# Revit family: 351_712 37 39
name_source: partatom
category: Plumbing Fixtures
revit_build: Autodesk Revit 2018 (Build: 20170223_1515(x64)
units: mm (PartAtom-declared; Revit-internal decimal feet)

## family parameters
Always vertical = Yes
Cut with Voids When Loaded = No
Part Type = Normal
Room Calculation Point = No
Round Connector Dimension = Use Diameter
Shared = No
Work Plane-Based = No

## types (1)
- ACO Golvbrunn 270 x 270 DN 75 Horizontal CB 9.5
    CAT0 = Yes
    CLBTZ = 0 mm  [stored 0 ft]
    CL_Location_5000 = 5000 mm  [stored 16.4042 ft]
    CT1 = No
    CT2 = Yes
    DC = 75 mm
    Description = ACO COLLECT BOX 9:5 EN1.4404 GULLY 270X270 H75 VINYL
    H2 = 60 mm  [stored 0.19685 ft]
    H4 = 8 mm  [stored 0.0262467 ft]
    H4_End__ve = -60 mm  [stored -0.19685 ft]
    H4__ve = -8 mm  [stored -0.0262467 ft]
    H5 = 52 mm  [stored 0.170604 ft]
    HTT = 157 mm  [stored 0.515092 ft]
    HTT__ve = -157 mm  [stored -0.515092 ft]
    LL = 130 mm  [stored 0.426509 ft]
    MC_Default_elevation = 0 mm  [stored 0 ft]
    Manufacturer = ACO Drain
    QmdConnectorList = 601;DC
    RR = 109 mm  [stored 0.357612 ft]
    WW = 130 mm  [stored 0.426509 ft]
    XRefLineVPlnId = 7453
    XX = 160 mm  [stored 0.524934 ft]
    YRefLineVPlnId = 7456
    YY = 160 mm  [stored 0.524934 ft]
    Z2 = 169 mm  [stored 0.554462 ft]
    magiPartTypeId = 351
    magiProductCode = ACO Golvbrunn 270 x 270 DN 75 Horizontal CB 9.5
    magiProductFamilyId = 712 37 39
    magiProductId = 712 37 39

note: [stored X ft] marks values corroborated as IEEE doubles in the binary element streams (Revit-internal decimal feet)

## geometry (parser evidence)
native form markers: Sweep x2
no freeform markers — native parametric forms only
